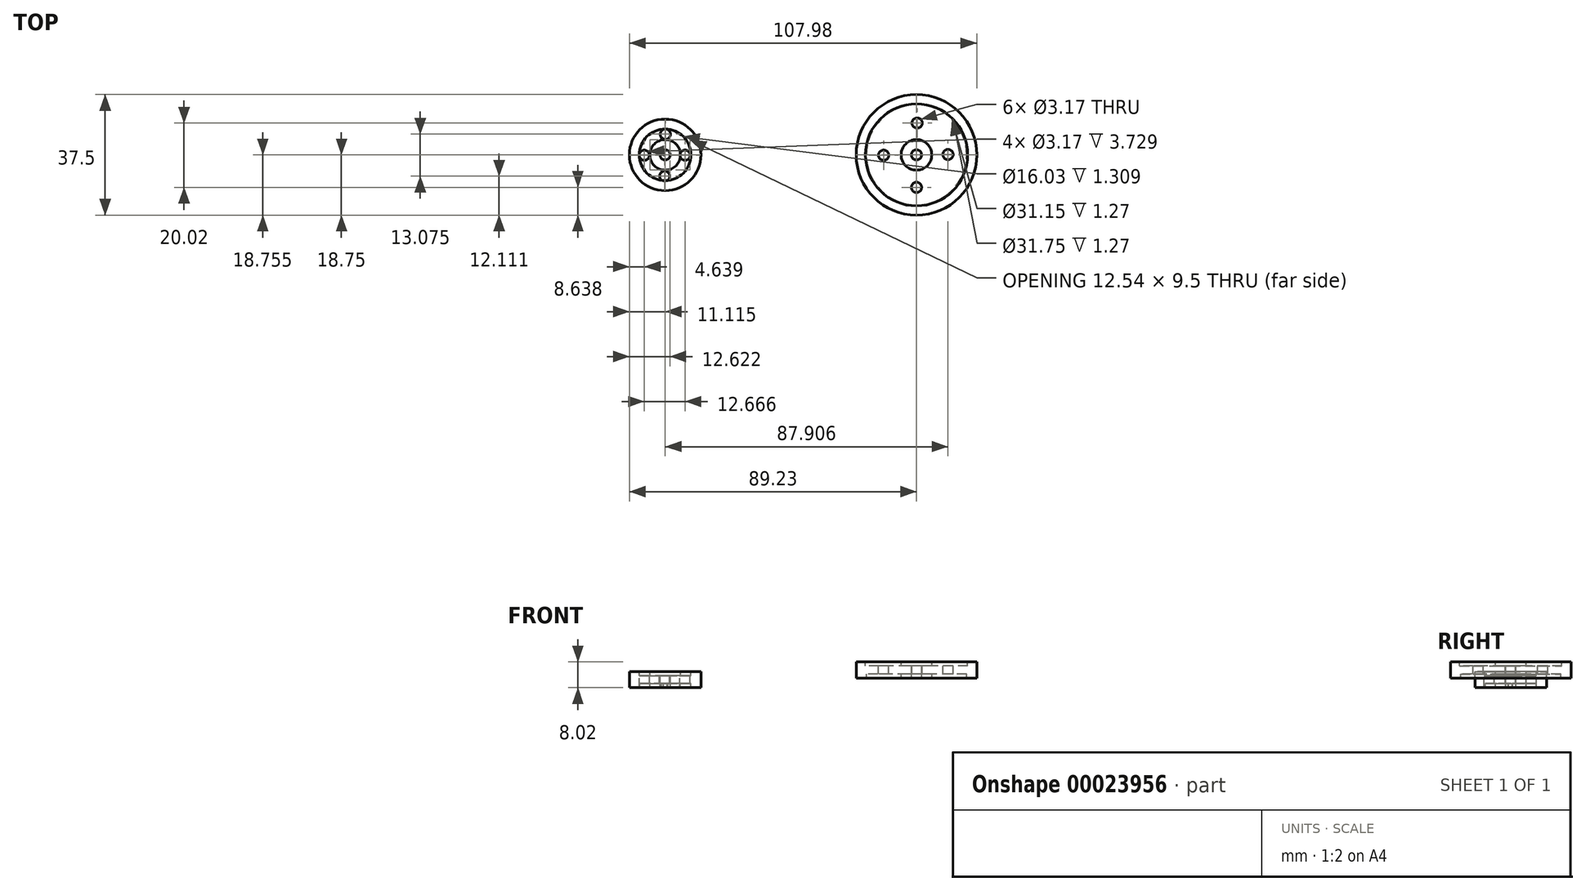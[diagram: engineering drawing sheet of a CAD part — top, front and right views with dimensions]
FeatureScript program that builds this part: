
annotation { "Feature Type Name" : "Feature", "Feature Type Description" : "" }
export const myFeature = defineFeature(function(context is Context, id is Id, definition is map)
    precondition{}
    {
        {
            var Q0;
            Q0=qCreatedBy(makeId("Front.planeOp"),FACE);
            var sketch = newSketch(context, id + "F0", { "sketchPlane" : qUnion([Q0])});
            skLineSegment(sketch, "E0", {"start": v(0, 41.27) * mm, "end": v(0, -51.72) * mm, "construction": true});
            skLineSegment(sketch, "E1", {"start": v(1.59, 3.73) * mm, "end": v(1.59, -1.27) * mm});
            skLineSegment(sketch, "E2", {"start": v(1.59, 3.73) * mm, "end": v(4.76, 3.73) * mm});
            skLineSegment(sketch, "E3", {"start": v(1.59, -1.27) * mm, "end": v(4.76, -1.27) * mm});
            skLineSegment(sketch, "E4", {"start": v(4.76, -1.27) * mm, "end": v(4.76, 0) * mm});
            skLineSegment(sketch, "E5", {"start": v(4.76, 3.73) * mm, "end": v(4.76, 2.46) * mm});
            skLineSegment(sketch, "E6", {"start": v(4.76, 0) * mm, "end": v(15.58, 0) * mm});
            skLineSegment(sketch, "E7", {"start": v(4.76, 2.46) * mm, "end": v(15.88, 2.46) * mm});
            skPoint(sketch, "E8", {"position": v(18.75, 3.73) * mm});
            skLineSegment(sketch, "E9", {"start": v(18.75, 3.73) * mm, "end": v(18.75, -1.27) * mm});
            skLineSegment(sketch, "E10", {"start": v(18.75, 3.73) * mm, "end": v(15.88, 3.73) * mm});
            skLineSegment(sketch, "E11", {"start": v(18.75, -1.27) * mm, "end": v(15.58, -1.27) * mm});
            skLineSegment(sketch, "E12", {"start": v(15.88, 3.73) * mm, "end": v(15.88, 2.46) * mm});
            skLineSegment(sketch, "E13", {"start": v(15.58, -1.27) * mm, "end": v(15.58, 0) * mm});
            skSolve(sketch);
        }
        {
            var Q0;
            Q0=makeQuery(id+"F0.imprint","IMPRINT",FACE,{"disambiguationData":[TD([[makeQuery(id+"F0.imprint","IMPRINT",EDGE,{"derivedFrom":sQuery(id+"F0.wireOp",EDGE,"E1")}),1.0]])]});
            var Q1;
            Q1=sQuery(id+"F0.wireOp",EDGE,"E0");
            revolve(context, id + "F1", {"entities" : qUnion([Q0]), "axis" : qUnion([Q1]), "revolveType" : RevolveType.FULL});
        }
        {
            var Q0;
            Q0=makeQuery(id+"F1.opRevolve","SWEPT_FACE",FACE,{"disambiguationData":[OSD([sQuery(id+"F0.wireOp",EDGE,"E7")])]});
            var sketch = newSketch(context, id + "F2", { "sketchPlane" : qUnion([Q0])});
            skCircle(sketch, "E14", {"center": v(0.19, 9.9) * mm, "radius": 1.59 * mm});
            skCircle(sketch, "E15", {"center": v(9.8, 0.1) * mm, "radius": 1.59 * mm});
            skCircle(sketch, "E16", {"center": v(0, -10.11) * mm, "radius": 1.59 * mm});
            skCircle(sketch, "E17", {"center": v(-10.23, -0.1) * mm, "radius": 1.59 * mm});
            skPoint(sketch, "E18.orphan", {"position": v(0.19, 18.7) * mm});
            skPoint(sketch, "E19.start.orphan", {"position": v(0, 0) * mm});
            skSolve(sketch);
        }
        {
            var Q0;
            Q0 = qSketchRegion(id + "F2", true);
            extrude(context, id + "F3", {"entities" : qUnion([Q0]), "operationType" : NewBodyOperationType.REMOVE, "oppositeDirection" : true, "depth" : 25.4 * mm});
        }
        {
            var Q0;
            Q0=qCreatedBy(makeId("Front.planeOp"),FACE);
            var sketch = newSketch(context, id + "F4", { "sketchPlane" : qUnion([Q0])});
            skLineSegment(sketch, "E20", {"start": v(-78.12, 43.13) * mm, "end": v(-78.12, -33.04) * mm, "construction": true});
            skPoint(sketch, "E21", {"position": v(-67, 0.75) * mm});
            skLineSegment(sketch, "E22", {"start": v(-73.35, -3.02) * mm, "end": v(-70.17, -3.02) * mm});
            skLineSegment(sketch, "E23", {"start": v(-73.35, -0.56) * mm, "end": v(-70.1, -0.56) * mm});
            skLineSegment(sketch, "E24", {"start": v(-76.53, 0.71) * mm, "end": v(-76.53, -4.29) * mm});
            skLineSegment(sketch, "E25", {"start": v(-76.53, -4.29) * mm, "end": v(-73.35, -4.29) * mm});
            skLineSegment(sketch, "E26", {"start": v(-73.35, -4.29) * mm, "end": v(-73.35, -3.02) * mm});
            skLineSegment(sketch, "E27", {"start": v(-67, 0.75) * mm, "end": v(-67, -4.29) * mm});
            skLineSegment(sketch, "E28", {"start": v(-70.17, -4.29) * mm, "end": v(-67, -4.29) * mm});
            skLineSegment(sketch, "E29", {"start": v(-70.1, 0.75) * mm, "end": v(-70.1, -0.56) * mm});
            skLineSegment(sketch, "E30", {"start": v(-70.17, -4.29) * mm, "end": v(-70.17, -3.02) * mm});
            skLineSegment(sketch, "E31", {"start": v(-76.53, 0.71) * mm, "end": v(-73.35, 0.71) * mm});
            skLineSegment(sketch, "E32", {"start": v(-73.35, 0.71) * mm, "end": v(-73.35, -0.56) * mm});
            skLineSegment(sketch, "E33", {"start": v(-67, 0.75) * mm, "end": v(-70.1, 0.75) * mm});
            skSolve(sketch);
        }
        {
            var Q0;
            Q0=makeQuery(id+"F4.imprint","IMPRINT",FACE,{"disambiguationData":[TD([[makeQuery(id+"F4.imprint","IMPRINT",EDGE,{"derivedFrom":sQuery(id+"F4.wireOp",EDGE,"E22")}),1.0]])]});
            var Q1;
            Q1=sQuery(id+"F4.wireOp",EDGE,"E20");
            revolve(context, id + "F5", {"entities" : qUnion([Q0]), "axis" : qUnion([Q1]), "revolveType" : RevolveType.FULL});
        }
        {
            var Q0;
            Q0=makeQuery(id+"F5.opRevolve","SWEPT_FACE",FACE,{"disambiguationData":[OSD([sQuery(id+"F4.wireOp",EDGE,"E23")])]});
            var sketch = newSketch(context, id + "F6", { "sketchPlane" : qUnion([Q0])});
            skCircle(sketch, "E34", {"center": v(-71.93, -0.1) * mm, "radius": 1.59 * mm});
            skCircle(sketch, "E35", {"center": v(-78.26, -6.64) * mm, "radius": 1.59 * mm});
            skCircle(sketch, "E36", {"center": v(-84.6, -0.1) * mm, "radius": 1.59 * mm});
            skCircle(sketch, "E37", {"center": v(-78.05, 6.44) * mm, "radius": 1.59 * mm});
            skSolve(sketch);
        }
        {
            var Q0;
            Q0 = qSketchRegion(id + "F6", true);
            extrude(context, id + "F7", {"entities" : qUnion([Q0]), "operationType" : NewBodyOperationType.REMOVE, "oppositeDirection" : true, "depth" : 25.4 * mm});
        }
    });
